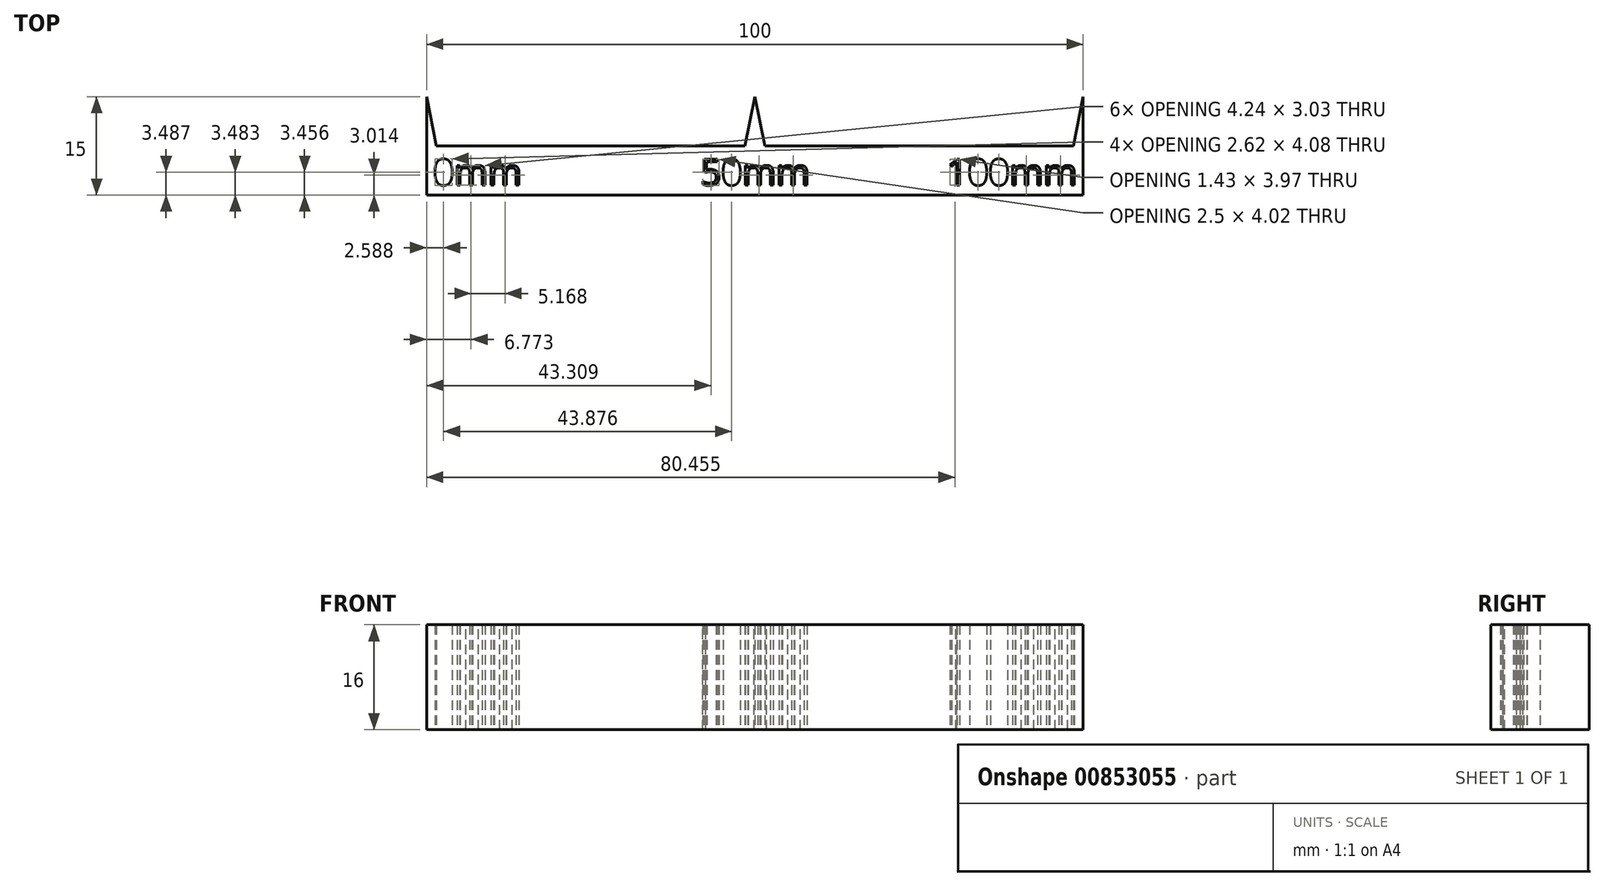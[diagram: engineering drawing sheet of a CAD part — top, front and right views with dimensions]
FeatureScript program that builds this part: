
annotation { "Feature Type Name" : "Feature", "Feature Type Description" : "" }
export const myFeature = defineFeature(function(context is Context, id is Id, definition is map)
    precondition{}
    {
        {
            var Q0;
            Q0=qCreatedBy(makeId("Top.planeOp"),FACE);
            var sketch = newSketch(context, id + "F0", { "sketchPlane" : qUnion([Q0])});
            skLineSegment(sketch, "E0.bottom", {"start": v(0, 0) * mm, "end": v(100, 0) * mm});
            skLineSegment(sketch, "E0.top", {"start": v(0, 15) * mm, "end": v(100, 15) * mm, "construction": true});
            skLineSegment(sketch, "E0.left", {"start": v(0, 0) * mm, "end": v(0, 15) * mm});
            skLineSegment(sketch, "E0.right", {"start": v(100, 0) * mm, "end": v(100, 15) * mm});
            skLineSegment(sketch, "E1", {"start": v(50, 15) * mm, "end": v(50, 0) * mm, "construction": true});
            skLineSegment(sketch, "E2", {"start": v(50, 15) * mm, "end": v(48.5, 7.5) * mm});
            skPoint(sketch, "E2.endSnap0", {"position": v(50, 7.5) * mm});
            skLineSegment(sketch, "E3", {"start": v(48.5, 7.5) * mm, "end": v(1.5, 7.5) * mm});
            skLineSegment(sketch, "E4", {"start": v(1.5, 7.5) * mm, "end": v(0, 15) * mm});
            skLineSegment(sketch, "E5", {"start": v(50, 15) * mm, "end": v(51.5, 7.5) * mm});
            skLineSegment(sketch, "E6", {"start": v(51.5, 7.5) * mm, "end": v(98.5, 7.5) * mm});
            skLineSegment(sketch, "E7", {"start": v(98.5, 7.5) * mm, "end": v(100, 15) * mm});
            skText(sketch, "E8", { "text": "0mm", "fontName": "OpenSans-Regular.ttf"});
            skText(sketch, "E9", { "text": "50mm", "fontName": "OpenSans-Regular.ttf"});
            skText(sketch, "E10", { "text": "100mm", "fontName": "OpenSans-Regular.ttf"});
            const initialGuessF0  = {"E8": [0.001, 0.0015, 1, 0, 0.004], "E9": [0.0417, 0.0015, 1, 0, 0.004], "E10": [0.07923, 0.0015, 1, 0, 0.004]};
            skSetInitialGuess(sketch, initialGuessF0);
            skSolve(sketch);
        }
        {
            var Q0;
            Q0 = qSketchRegion(id + "F0", true);
            extrude(context, id + "F1", {"entities" : qUnion([Q0]), "depth" : 16 * mm, "offsetDistance" : 25 * mm});
        }
    });
